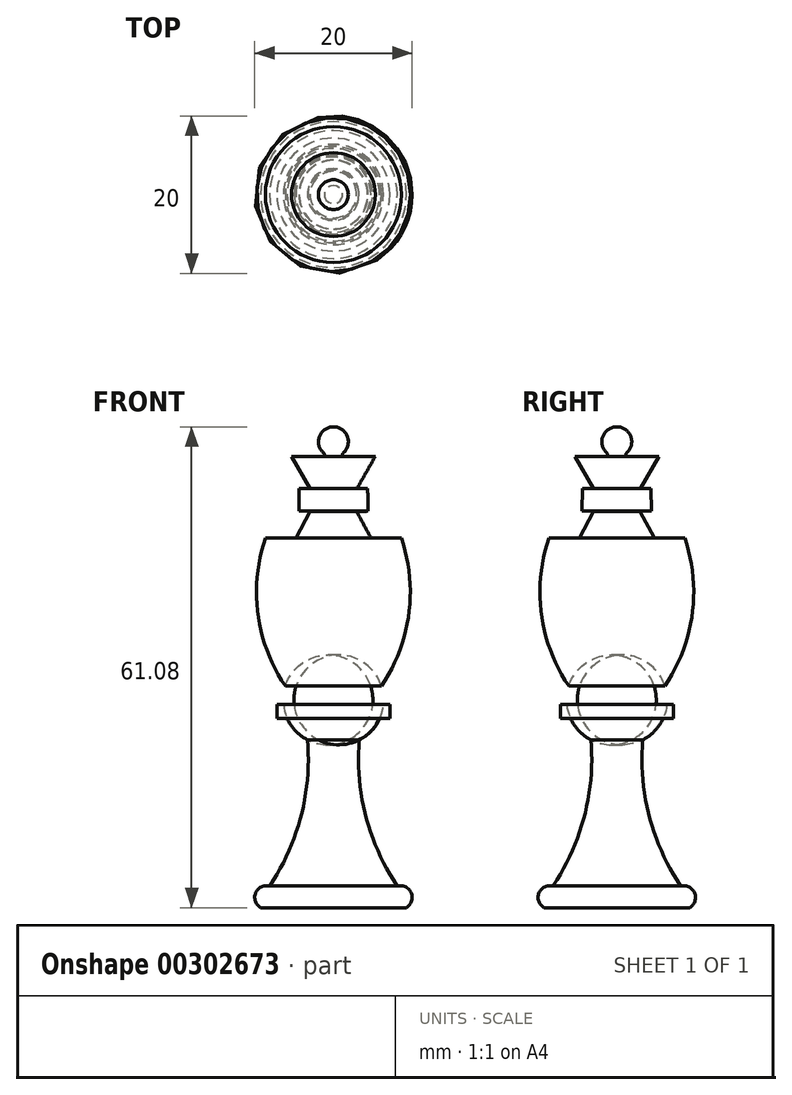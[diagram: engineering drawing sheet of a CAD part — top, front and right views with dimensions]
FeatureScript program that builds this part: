
annotation { "Feature Type Name" : "Feature", "Feature Type Description" : "" }
export const myFeature = defineFeature(function(context is Context, id is Id, definition is map)
    precondition{}
    {
        {
            var Q0;
            Q0=qCreatedBy(makeId("Front.planeOp"),FACE);
            var sketch = newSketch(context, id + "F0", { "sketchPlane" : qUnion([Q0])});
            skLineSegment(sketch, "E0", {"start": v(0, 61.76) * mm, "end": v(0, -15.37) * mm});
            skLineSegment(sketch, "E1", {"start": v(-5.32, 54.59) * mm, "end": v(0, 54.59) * mm});
            skLineSegment(sketch, "E2", {"start": v(-5.32, 54.59) * mm, "end": v(-2.96, 50.45) * mm});
            skLineSegment(sketch, "E3.bottom", {"start": v(-2.96, 47.56) * mm, "end": v(-4.4, 47.62) * mm});
            skLineSegment(sketch, "E3.right", {"start": v(-4.4, 47.62) * mm, "end": v(-4.35, 50.5) * mm});
            skPoint(sketch, "E3.middle", {"position": v(0, 48.87) * mm});
            skLineSegment(sketch, "E4", {"start": v(-2.96, 47.56) * mm, "end": v(-4.77, 44.23) * mm});
            skLineSegment(sketch, "E5", {"start": v(-8.63, 44.23) * mm, "end": v(-4.77, 44.23) * mm});
            skArc(sketch, "E6", {"start": v(-8.63, 44.23) * mm, "mid": v(-9.58, 34.53) * mm, "end": v(-6.1, 25.42) * mm});
            skArc(sketch, "E7", {"start": v(-6.1, 25.42) * mm, "mid": v(-6.36, 24.25) * mm, "end": v(-6.36, 23.05) * mm});
            skLineSegment(sketch, "E8", {"start": v(-6.36, 23.05) * mm, "end": v(-7.17, 23.05) * mm});
            skLineSegment(sketch, "E9", {"start": v(-7.17, 23.05) * mm, "end": v(-7.17, 21.27) * mm});
            skLineSegment(sketch, "E10", {"start": v(-7.17, 21.27) * mm, "end": v(-5.87, 21.27) * mm});
            skPoint(sketch, "E11.end.orphan", {"position": v(3.15, 50.45) * mm});
            skPoint(sketch, "E3.left.end.orphan", {"position": v(4.4, 50.12) * mm});
            skPoint(sketch, "E3.left.start.orphan", {"position": v(4.35, 47.25) * mm});
            skPoint(sketch, "E12.trimOffspring.end.orphan", {"position": v(4.73, 25.42) * mm});
            skArc(sketch, "E13", {"start": v(0, 58.34) * mm, "mid": v(-1.9, 56.45) * mm, "end": v(0, 54.55) * mm});
            skArc(sketch, "E14.trimOffspring", {"start": v(-5.87, 21.27) * mm, "mid": v(-4.8, 19.7) * mm, "end": v(-3.28, 18.57) * mm});
            skArc(sketch, "E15", {"start": v(-8.11, 0) * mm, "mid": v(-4.12, 8.88) * mm, "end": v(-3.28, 18.57) * mm});
            skArc(sketch, "E16", {"start": v(-8.11, 0) * mm, "mid": v(-9.88, -0.87) * mm, "end": v(-9.26, -2.74) * mm});
            skLineSegment(sketch, "E17", {"start": v(-9.26, -2.74) * mm, "end": v(0, -2.74) * mm});
            skLineSegment(sketch, "E18", {"start": v(-4.35, 50.5) * mm, "end": v(-2.96, 50.45) * mm});
            skSolve(sketch);
        }
        {
            var Q0;
            {var subQ0=sQuery(id+"F0.wireOp",EDGE,"E1");var subQ1=sQuery(id+"F0.wireOp",EDGE,"E0");var subQ2=makeQuery(id+"F0.imprint","INTERSECT",VERTEX,{"derivedFrom":[subQ1,subQ0]});Q0=makeQuery(id+"F0.imprint","IMPRINT",FACE,{"disambiguationData":[TD([[makeQuery(id+"F0.imprint","IMPRINT",EDGE,{"disambiguationData":[TD([[subQ2,1.0]])],"derivedFrom":subQ1}),-1.0]])]});}
            var Q1;
            {var subQ0=sQuery(id+"F0.wireOp",EDGE,"E1");var subQ1=sQuery(id+"F0.wireOp",EDGE,"E0");var subQ2=makeQuery(id+"F0.imprint","INTERSECT",VERTEX,{"derivedFrom":[subQ1,subQ0]});Q1=makeQuery(id+"F0.imprint","IMPRINT",FACE,{"disambiguationData":[TD([[makeQuery(id+"F0.imprint","IMPRINT",EDGE,{"disambiguationData":[TD([[subQ2,-1.0]])],"derivedFrom":subQ1}),-1.0]])]});}
            var Q2;
            {var subQ4=sQuery(id+"F0.wireOp",EDGE,"E2");Q2=makeQuery(id+"F0.imprint","IMPRINT",FACE,{"disambiguationData":[TD([[makeQuery(id+"F0.imprint","IMPRINT",EDGE,{"derivedFrom":subQ4}),1.0]])]});}
            var Q3;
            Q3=sQuery(id+"F0.wireOp",EDGE,"E0");
            revolve(context, id + "F1", {"entities" : qUnion([Q0, Q1, Q2]), "axis" : qUnion([Q3]), "revolveType" : RevolveType.FULL});
        }
        {
            var Q0;
            Q0=makeQuery(id+"F1.opRevolve","SWEPT_EDGE",EDGE,{"disambiguationData":[OSD([sQuery(id+"F0.wireOp",EDGE,"E1"),sQuery(id+"F0.wireOp",EDGE,"E13")])]});
            fillet(context, id + "F2", {"entities" : qUnion([Q0]), "radius" : 0.24 * mm, "tangentPropagation" : true, "allowEdgeOverflow" : false});
        }
    });
